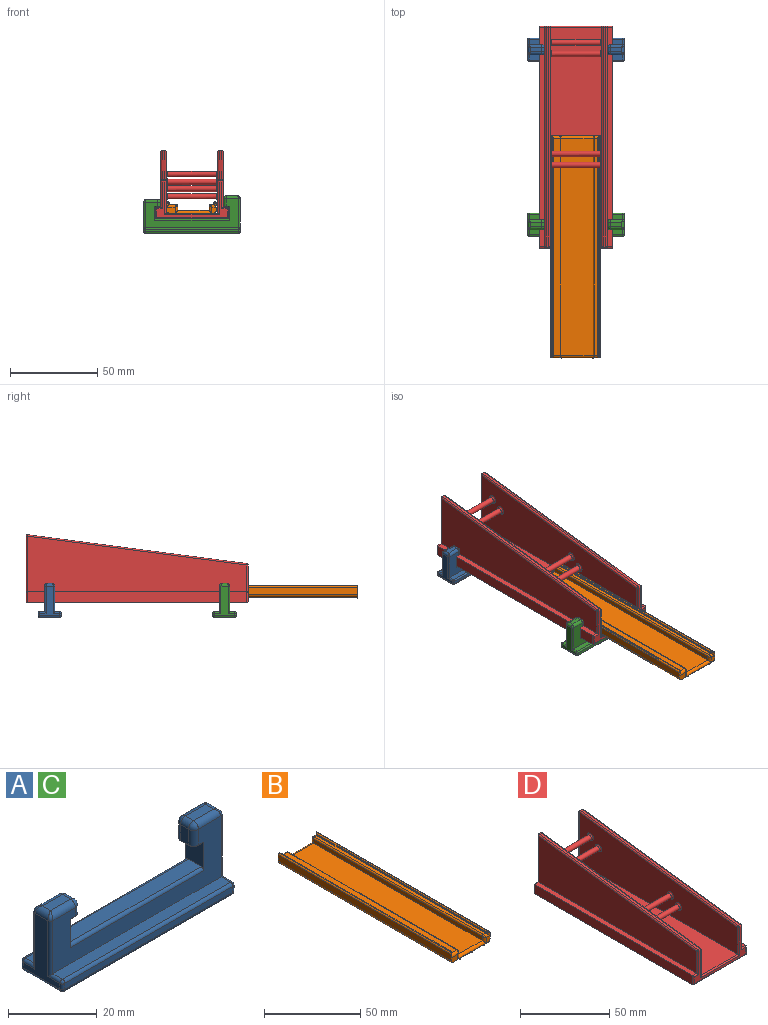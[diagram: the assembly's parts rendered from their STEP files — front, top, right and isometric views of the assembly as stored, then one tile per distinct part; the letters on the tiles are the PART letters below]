
ASSEMBLY  parts=4 mates=3
PART A: 76 faces, bbox 55.1x13.3x21.4 mm
  f0: plane 53.49x16.69mm, normal (0,-1,0), area 372.4mm2, adj f9,f11,f17,f18,f23,f28,f30,f35
  f1: plane 2.57x2.36mm, normal (1,0,0), area 6.1mm2, adj f16,f17,f21,f32
  f2: plane 6.38x2.57mm, normal (0,0,1), area 16.4mm2, adj f14,f15,f18,f21
  f3: plane 17.04x11.76mm, normal (-1,0,0), area 82.8mm2, adj f14,f45,f46,f50,f56,f59,f62,f63
  f4: plane 53.49x11.76mm, normal (0,0,-1), area 629.1mm2, adj f56,f57,f64,f65
  f5: plane 19.08x11.76mm, normal (1,0,0), area 91.2mm2, adj f29,f49,f52,f58,f65,f69,f71,f72
  f6: plane 6.38x2.57mm, normal (0,0,1), area 16.4mm2, adj f24,f27,f28,f29
  f7: plane 4.39x2.57mm, normal (-1,0,0), area 11.3mm2, adj f22,f23,f24,f37
  f8: plane 4.95x2.79mm, normal (0,0,-1), area 13.2mm2, adj f9,f35,f36,f37,f38,f39
  f9: plane 7.87x5.72mm, normal (-1,0,0), area 38.7mm2, adj f0,f8,f10,f13,f35,f39,f74,f75
  f10: plane 42.37x4.14mm, normal (0,0,1), area 175.4mm2, adj f9,f11,f74,f75
  f11: plane 7.87x5.72mm, normal (1,0,0), area 38.7mm2, adj f0,f10,f12,f13,f30,f34,f74,f75
  f12: plane 4.95x2.79mm, normal (0,0,-1), area 13.2mm2, adj f11,f30,f31,f32,f33,f34
  f13: plane 53.49x16.69mm, normal (0,1,0), area 372.4mm2, adj f9,f11,f15,f16,f22,f27,f34,f39
  f14: cylinder r=1.57mm len=4.14mm, axis (0,-1,0), area 8.8mm2, adj f2,f3,f44,f55
  f15: cylinder r=1.57mm len=7.16mm, axis (1,0,0), area 17mm2, adj f2,f13,f19,f55
  f16: cylinder r=1.57mm len=2.36mm, axis (0,0,-1), area 5.8mm2, adj f1,f13,f19,f33
  f17: cylinder r=1.57mm len=2.36mm, axis (0,0,1), area 5.8mm2, adj f0,f1,f20,f31
  f18: cylinder r=1.57mm len=7.16mm, axis (-1,0,0), area 17mm2, adj f0,f2,f20,f44
  f19: sphere r=1.57mm, area 3.9mm2, adj f15,f16,f21
  f20: sphere r=1.57mm, area 3.9mm2, adj f17,f18,f21
  f21: cylinder r=1.57mm len=2.57mm, axis (0,1,0), area 6.3mm2, adj f1,f2,f19,f20
  f22: cylinder r=1.57mm len=4.39mm, axis (0,0,1), area 10.9mm2, adj f7,f13,f25,f38
  f23: cylinder r=1.57mm len=4.39mm, axis (0,0,-1), area 10.9mm2, adj f0,f7,f26,f36
  f24: cylinder r=1.57mm len=2.57mm, axis (0,1,0), area 6.3mm2, adj f6,f7,f25,f26
  f25: sphere r=1.57mm, area 3.9mm2, adj f22,f24,f27
  f26: sphere r=1.57mm, area 3.9mm2, adj f23,f24,f28
  f27: cylinder r=1.57mm len=7.16mm, axis (1,0,0), area 17mm2, adj f6,f13,f25,f73
  f28: cylinder r=1.57mm len=7.16mm, axis (-1,0,0), area 17mm2, adj f0,f6,f26,f47
  f29: cylinder r=1.57mm len=4.14mm, axis (0,-1,0), area 8.8mm2, adj f5,f6,f47,f73
  f30: plane 1.6x0.38mm, normal (0,-0.71,-0.71), area 0.9mm2, adj f0,f11,f12,f31
  f31: cone r=1.19mm half-angle=45deg, axis (0,0,1), area 1.2mm2, adj f12,f17,f30,f32
  f32: plane 2.57x0.38mm, normal (0.71,0,-0.71), area 1.4mm2, adj f1,f12,f31,f33
  f33: cone r=1.19mm half-angle=45deg, axis (0,0,1), area 1.2mm2, adj f12,f16,f32,f34
  f34: plane 1.6x0.38mm, normal (0,0.71,-0.71), area 0.9mm2, adj f11,f12,f13,f33
  f35: plane 1.6x0.38mm, normal (0,-0.71,-0.71), area 0.9mm2, adj f0,f8,f9,f36
  f36: cone r=1.19mm half-angle=45deg, axis (0,0,1), area 1.2mm2, adj f8,f23,f35,f37
  f37: plane 2.57x0.38mm, normal (-0.71,0,-0.71), area 1.4mm2, adj f7,f8,f36,f38
  f38: cone r=1.19mm half-angle=45deg, axis (0,0,1), area 1.2mm2, adj f8,f22,f37,f39
  f39: plane 1.6x0.38mm, normal (0,0.71,-0.71), area 0.9mm2, adj f8,f9,f13,f38
  f40: plane 53.49x1.6mm, normal (0,-1,0), area 85.6mm2, adj f50,f51,f57,f58
  f41: plane 53.49x3.02mm, normal (0,0,1), area 161.7mm2, adj f0,f46,f51,f52
  f42: plane 53.49x1.6mm, normal (0,1,0), area 85.6mm2, adj f63,f64,f68,f69
  f43: plane 53.49x3.02mm, normal (0,0,1), area 161.7mm2, adj f13,f62,f68,f71
  f44: bspline ~1.88x1.57mm, area 2mm2, adj f14,f18,f45
  f45: cylinder r=0.79mm len=15.44mm, axis (0,0,-1), area 18.5mm2, adj f0,f3,f44,f46
  f46: cylinder r=0.79mm len=3.81mm, axis (0,1,0), area 4.1mm2, adj f3,f41,f45,f48
  f47: bspline ~1.88x1.58mm, area 2mm2, adj f28,f29,f49
  f48: sphere r=0.79mm, area 1mm2, adj f46,f50,f51
  f49: cylinder r=0.79mm len=17.48mm, axis (0,0,1), area 21mm2, adj f0,f5,f47,f52
  f50: cylinder r=0.79mm len=1.6mm, axis (0,0,1), area 2mm2, adj f3,f40,f48,f53
  f51: cylinder r=0.79mm len=53.49mm, axis (-1,0,0), area 66.2mm2, adj f40,f41,f48,f54
  f52: cylinder r=0.79mm len=3.81mm, axis (0,-1,0), area 4.1mm2, adj f5,f41,f49,f54
  f53: sphere r=0.79mm, area 1mm2, adj f50,f56,f57
  f54: sphere r=0.79mm, area 1mm2, adj f51,f52,f58
  f55: bspline ~1.88x1.57mm, area 2mm2, adj f14,f15,f59
  f56: cylinder r=0.79mm len=11.76mm, axis (0,-1,0), area 14.5mm2, adj f3,f4,f53,f60
  f57: cylinder r=0.79mm len=53.49mm, axis (1,0,0), area 66.2mm2, adj f4,f40,f53,f61
  f58: cylinder r=0.79mm len=1.6mm, axis (0,0,-1), area 2mm2, adj f5,f40,f54,f61
  f59: cylinder r=0.79mm len=15.44mm, axis (0,0,1), area 18.5mm2, adj f3,f13,f55,f62
  f60: sphere r=0.79mm, area 1mm2, adj f56,f63,f64
  f61: sphere r=0.79mm, area 1mm2, adj f57,f58,f65
  f62: cylinder r=0.79mm len=3.81mm, axis (0,1,0), area 4.1mm2, adj f3,f43,f59,f66
  f63: cylinder r=0.79mm len=1.6mm, axis (0,0,-1), area 2mm2, adj f3,f42,f60,f66
  f64: cylinder r=0.79mm len=53.49mm, axis (-1,0,0), area 66.2mm2, adj f4,f42,f60,f67
  f65: cylinder r=0.79mm len=11.76mm, axis (0,1,0), area 14.5mm2, adj f4,f5,f61,f67
  f66: sphere r=0.79mm, area 1mm2, adj f62,f63,f68
  f67: sphere r=0.79mm, area 1mm2, adj f64,f65,f69
  f68: cylinder r=0.79mm len=53.49mm, axis (-1,0,0), area 66.2mm2, adj f42,f43,f66,f70
  f69: cylinder r=0.79mm len=1.6mm, axis (0,0,1), area 2mm2, adj f5,f42,f67,f70
  f70: sphere r=0.79mm, area 1mm2, adj f68,f69,f71
  f71: cylinder r=0.79mm len=3.81mm, axis (0,-1,0), area 4.1mm2, adj f5,f43,f70,f72
  f72: cylinder r=0.79mm len=17.48mm, axis (0,0,-1), area 21mm2, adj f5,f13,f71,f73
  f73: bspline ~1.88x1.57mm, area 2mm2, adj f27,f29,f72
  f74: cylinder r=0.79mm len=42.37mm, axis (-1,0,0), area 52.4mm2, adj f0,f9,f10,f11
  f75: cylinder r=0.79mm len=42.37mm, axis (1,0,0), area 52.4mm2, adj f9,f10,f11,f13
PART B: 58 faces, bbox 28.5x127x6.9 mm
  f0: plane 123.85x17.78mm, normal (0,0,1), area 2202.1mm2, adj f1,f23,f32,f41
  f1: plane 123.85x2.62mm, normal (1,0,0), area 324mm2, adj f0,f26,f33,f42
  f2: plane 123.85x4.14mm, normal (0,0,1), area 512.8mm2, adj f3,f26,f36,f45
  f3: plane 123.85x0.51mm, normal (1,0,0), area 62.9mm2, adj f2,f4,f34,f43
  f4: plane 126.58x0.79mm, normal (0,0,1), area 99mm2, adj f3,f5,f34,f43
  f5: plane 126.58x0.51mm, normal (1,0,0), area 64.3mm2, adj f4,f6,f34,f43
  f6: plane 126.58x0.79mm, normal (0,0,-1), area 99mm2, adj f5,f27,f34,f43
  f7: plane 126.55x0.12mm, normal (0,0,1), area 14.9mm2, adj f27,f28,f34,f43
  f8: plane 127x3.96mm, normal (-1,0,0), area 503.2mm2, adj f24,f25,f28,f34,f43,f50
  f9: plane 127x4.11mm, normal (0,0,-1), area 521.7mm2, adj f24,f25,f50,f52
  f10: cylinder r=0.55mm len=127mm, axis (0,-1,0), area 159.1mm2, adj f24,f25,f52,f53
  f11: plane 127x7.2mm, normal (0,0,-1), area 914.4mm2, adj f24,f25,f53,f54
  f12: cylinder r=0.55mm len=127mm, axis (0,-1,0), area 159.1mm2, adj f24,f25,f54,f55
  f13: plane 127x7.2mm, normal (0,0,-1), area 914.4mm2, adj f24,f25,f55,f56
  f14: cylinder r=0.55mm len=127mm, axis (0,-1,0), area 159.1mm2, adj f24,f25,f56,f57
  f15: plane 127x1.82mm, normal (0,0,-1), area 231.4mm2, adj f24,f25,f51,f57
  f16: plane 127x3.96mm, normal (1,0,0), area 503.2mm2, adj f24,f25,f29,f37,f46,f51
  f17: plane 126.55x0.12mm, normal (0,0,1), area 14.9mm2, adj f29,f30,f37,f46
  f18: plane 126.58x0.79mm, normal (0,0,-1), area 99mm2, adj f19,f30,f37,f46
  f19: plane 126.58x0.51mm, normal (-1,0,0), area 64.3mm2, adj f18,f20,f37,f46
  f20: plane 126.58x0.79mm, normal (0,0,1), area 99mm2, adj f19,f21,f37,f46
  f21: plane 123.85x0.51mm, normal (-1,0,0), area 62.9mm2, adj f20,f22,f37,f46
  f22: plane 123.85x1.85mm, normal (0,0,1), area 229.6mm2, adj f21,f31,f38,f49
  f23: plane 123.85x2.62mm, normal (-1,0,0), area 324mm2, adj f0,f31,f40,f47
  f24: plane 28.55x3.99mm, normal (0,1,0), area 26.9mm2, adj f8,f9,f10,f11,f12,f13,f14,f15
  f25: plane 28.55x3.99mm, normal (0,-1,0), area 26.9mm2, adj f8,f9,f10,f11,f12,f13,f14,f15
  f26: cylinder r=0.81mm len=123.85mm, axis (0,-1,0), area 158.1mm2, adj f1,f2,f35,f44
  f27: cylinder r=0.81mm len=126.39mm, axis (0,1,0), area 93.4mm2, adj f6,f7,f34,f43
  f28: cylinder r=0.81mm len=127mm, axis (0,-1,0), area 162mm2, adj f7,f8,f34,f43
  f29: cylinder r=0.81mm len=127mm, axis (0,-1,0), area 162mm2, adj f16,f17,f37,f46
  f30: cylinder r=0.81mm len=126.39mm, axis (0,1,0), area 93.4mm2, adj f17,f18,f37,f46
  f31: cylinder r=0.81mm len=123.85mm, axis (0,-1,0), area 158.1mm2, adj f22,f23,f39,f48
  f32: cylinder r=1.57mm len=20.93mm, axis (1,0,0), area 46.8mm2, adj f0,f24,f33,f47
  f33: cylinder r=1.57mm len=4.19mm, axis (0,0,-1), area 7.2mm2, adj f1,f24,f32,f35
  f34: cylinder r=1.57mm len=2.91mm, axis (0,0,-1), area 3.5mm2, adj f3,f4,f5,f6,f7,f8,f27,f28
  f35: bspline ~1.65x1.58mm, area 2.1mm2, adj f26,f33,f36
  f36: cylinder r=1.57mm len=5.72mm, axis (1,0,0), area 11mm2, adj f2,f24,f34,f35
  f37: cylinder r=1.57mm len=2.91mm, axis (0,0,-1), area 3.5mm2, adj f16,f17,f18,f19,f20,f21,f29,f30
  f38: cylinder r=1.57mm len=3.43mm, axis (-1,0,0), area 5.3mm2, adj f22,f25,f37,f39
  f39: bspline ~1.65x1.58mm, area 2.1mm2, adj f31,f38,f40
  f40: cylinder r=1.57mm len=4.19mm, axis (0,0,-1), area 7.2mm2, adj f23,f25,f39,f41
  f41: cylinder r=1.57mm len=20.93mm, axis (-1,0,0), area 46.8mm2, adj f0,f25,f40,f42
  f42: cylinder r=1.57mm len=4.19mm, axis (0,0,1), area 7.2mm2, adj f1,f25,f41,f44
  f43: cylinder r=1.57mm len=2.91mm, axis (0,0,1), area 3.5mm2, adj f3,f4,f5,f6,f7,f8,f27,f28
  f44: bspline ~1.65x1.58mm, area 2.1mm2, adj f26,f42,f45
  f45: cylinder r=1.57mm len=5.72mm, axis (-1,0,0), area 11mm2, adj f2,f25,f43,f44
  f46: cylinder r=1.57mm len=2.91mm, axis (0,0,1), area 3.5mm2, adj f16,f17,f18,f19,f20,f21,f29,f30
  f47: cylinder r=1.57mm len=4.19mm, axis (0,0,1), area 7.2mm2, adj f23,f24,f32,f48
  f48: bspline ~1.65x1.58mm, area 2.1mm2, adj f31,f47,f49
  f49: cylinder r=1.57mm len=3.43mm, axis (1,0,0), area 5.3mm2, adj f22,f24,f46,f48
  f50: cylinder r=1.57mm len=127mm, axis (0,1,0), area 314.2mm2, adj f8,f9,f24,f25
  f51: cylinder r=1.57mm len=127mm, axis (0,1,0), area 314.2mm2, adj f15,f16,f24,f25
  f52: cylinder r=0.38mm len=127mm, axis (0,-1,0), area 55.5mm2, adj f9,f10,f24,f25
  f53: cylinder r=0.38mm len=127mm, axis (0,-1,0), area 55.5mm2, adj f10,f11,f24,f25
  f54: cylinder r=0.38mm len=127mm, axis (0,-1,0), area 55.5mm2, adj f11,f12,f24,f25
  f55: cylinder r=0.38mm len=127mm, axis (0,-1,0), area 55.5mm2, adj f12,f13,f24,f25
  f56: cylinder r=0.38mm len=127mm, axis (0,-1,0), area 55.5mm2, adj f13,f14,f24,f25
  f57: cylinder r=0.38mm len=127mm, axis (0,-1,0), area 55.5mm2, adj f14,f15,f24,f25
PART C: same geometry as A
PART D: 61 faces, bbox 42x127x38.8 mm
  f0: plane 125.37x6.35mm, normal (-1,0,0), area 796.1mm2, adj f1,f9,f28,f32
  f1: plane 125.37x42.01mm, normal (0,0,-1), area 5267.2mm2, adj f0,f2,f24,f27
  f2: plane 126.19x6.35mm, normal (1,0,0), area 801mm2, adj f1,f3,f10,f18,f23,f24
  f3: plane 125.37x3.18mm, normal (0,0,1), area 398.1mm2, adj f2,f4,f18,f19
  f4: plane 125.37x31.67mm, normal (1,0,0), area 2935.7mm2, adj f3,f20,f21,f22
  f5: plane 125.37x34.84mm, normal (-1,0,0), area 3261.3mm2, adj f6,f30,f38,f39,f53,f55,f57,f59
  f6: plane 125.37x29.31mm, normal (0,0,1), area 3674.9mm2, adj f5,f7,f43,f44
  f7: plane 125.37x34.84mm, normal (1,0,0), area 3261.3mm2, adj f6,f47,f48,f52,f54,f56,f58,f60
  f8: plane 125.37x31.67mm, normal (-1,0,0), area 2935.7mm2, adj f9,f37,f40,f41
  f9: plane 125.37x3.18mm, normal (0,0,1), area 398.1mm2, adj f0,f8,f33,f36
  f10: plane 41.2x37.21mm, normal (0,1,0), area 197.1mm2, adj f2,f18,f20,f24,f28,f29,f33,f37
  f11: plane 40.39x20.7mm, normal (0,-1,0), area 142.1mm2, adj f19,f22,f23,f27,f31,f32,f36,f39
  f12: cylinder r=1.59mm len=27.69mm, axis (-1,0,0), area 276.2mm2, adj f59,f60
  f13: cylinder r=1.59mm len=27.69mm, axis (-1,0,0), area 276.2mm2, adj f57,f58
  f14: cylinder r=1.59mm len=27.69mm, axis (-1,0,0), area 276.2mm2, adj f55,f56
  f15: cylinder r=1.59mm len=27.69mm, axis (-1,0,0), area 276.2mm2, adj f53,f54
  f16: plane 125.37x16.51mm, normal (0,-0.13,0.99), area 195.9mm2, adj f21,f29,f30,f31
  f17: plane 125.37x16.51mm, normal (0,-0.13,0.99), area 195.9mm2, adj f41,f46,f49,f52
  f18: cylinder r=0.81mm len=3.99mm, axis (1,0,0), area 4.4mm2, adj f2,f3,f10,f20
  f19: cylinder r=0.81mm len=3.99mm, axis (-1,0,0), area 4.1mm2, adj f3,f11,f22,f23
  f20: cylinder r=0.81mm len=32.48mm, axis (0,0,-1), area 40.8mm2, adj f4,f10,f18,f25
  f21: cylinder r=0.81mm len=125.48mm, axis (0,-0.99,-0.13), area 161.5mm2, adj f4,f16,f25,f26
  f22: cylinder r=0.81mm len=15.98mm, axis (0,0,1), area 19.7mm2, adj f4,f11,f19,f26
  f23: cylinder r=0.81mm len=6.35mm, axis (0,0,1), area 7.4mm2, adj f2,f11,f19,f27
  f24: cylinder r=0.81mm len=42.01mm, axis (-1,0,0), area 53.3mm2, adj f1,f2,f10,f28
  f25: sphere r=0.81mm, area 1.1mm2, adj f20,f21,f29
  f26: sphere r=0.81mm, area 1mm2, adj f21,f22,f31
  f27: cylinder r=0.81mm len=42.01mm, axis (1,0,0), area 52.9mm2, adj f1,f11,f23,f32
  f28: cylinder r=0.81mm len=6.35mm, axis (0,0,1), area 7.4mm2, adj f0,f10,f24,f33
  f29: cylinder r=0.81mm len=1.55mm, axis (1,0,0), area 2.1mm2, adj f10,f16,f25,f34
  f30: cylinder r=0.81mm len=125.48mm, axis (0,0.99,0.13), area 161.5mm2, adj f5,f16,f34,f35
  f31: cylinder r=0.81mm len=1.55mm, axis (-1,0,0), area 1.8mm2, adj f11,f16,f26,f35
  f32: cylinder r=0.81mm len=6.35mm, axis (0,0,-1), area 7.4mm2, adj f0,f11,f27,f36
  f33: cylinder r=0.81mm len=3.99mm, axis (1,0,0), area 4.1mm2, adj f9,f10,f28,f37
  f34: sphere r=0.81mm, area 1.1mm2, adj f29,f30,f38
  f35: sphere r=0.81mm, area 1mm2, adj f30,f31,f39
  f36: cylinder r=0.81mm len=3.99mm, axis (-1,0,0), area 4.1mm2, adj f9,f11,f32,f40
  f37: cylinder r=0.81mm len=32.48mm, axis (0,0,1), area 40.8mm2, adj f8,f10,f33,f42
  f38: cylinder r=0.81mm len=35.66mm, axis (0,0,1), area 44.9mm2, adj f5,f10,f34,f43
  f39: cylinder r=0.81mm len=19.15mm, axis (0,0,-1), area 23.8mm2, adj f5,f11,f35,f44
  f40: cylinder r=0.81mm len=15.98mm, axis (0,0,-1), area 19.7mm2, adj f8,f11,f36,f45
  f41: cylinder r=0.81mm len=125.48mm, axis (0,0.99,0.13), area 161.5mm2, adj f8,f17,f42,f45
  f42: sphere r=0.81mm, area 1.1mm2, adj f37,f41,f46
  f43: cylinder r=0.81mm len=30.94mm, axis (1,0,0), area 38.2mm2, adj f6,f10,f38,f47
  f44: cylinder r=0.81mm len=30.94mm, axis (-1,0,0), area 38.2mm2, adj f6,f11,f39,f48
  f45: sphere r=0.81mm, area 1mm2, adj f40,f41,f49
  f46: cylinder r=0.81mm len=1.55mm, axis (1,0,0), area 2.1mm2, adj f10,f17,f42,f50
  f47: cylinder r=0.81mm len=35.66mm, axis (0,0,-1), area 44.9mm2, adj f7,f10,f43,f50
  f48: cylinder r=0.81mm len=19.15mm, axis (0,0,1), area 23.8mm2, adj f7,f11,f44,f51
  f49: cylinder r=0.81mm len=1.55mm, axis (-1,0,0), area 1.8mm2, adj f11,f17,f45,f51
  f50: sphere r=0.81mm, area 1.1mm2, adj f46,f47,f52
  f51: sphere r=0.81mm, area 1mm2, adj f48,f49,f52
  f52: cylinder r=0.81mm len=125.48mm, axis (0,-0.99,-0.13), area 161.5mm2, adj f7,f17,f50,f51
  f53: torus R=2.4mm, axis (1,0,0), area 15.1mm2, adj f5,f15
  f54: torus R=2.4mm, axis (-1,0,0), area 15.1mm2, adj f7,f15
  f55: torus R=2.4mm, axis (1,0,0), area 15.1mm2, adj f5,f14
  f56: torus R=2.4mm, axis (-1,0,0), area 15.1mm2, adj f7,f14
  f57: torus R=2.4mm, axis (1,0,0), area 15.1mm2, adj f5,f13
  f58: torus R=2.4mm, axis (-1,0,0), area 15.1mm2, adj f7,f13
  f59: torus R=2.4mm, axis (1,0,0), area 15.1mm2, adj f5,f12
  f60: torus R=2.4mm, axis (-1,0,0), area 15.1mm2, adj f7,f12
PLACE A t=(1.71,73.59,23.51)mm
PLACE B t=(1.41,-99.73,22.95)mm
PLACE C t=(1.71,-26.39,23.51)mm
PLACE D t=(1.71,-37.04,23.33)mm fixed
MATE fastened D.f6 <-> B.f11  axis (0,0,1) through (0.57,-36.23,22.95)mm
MATE fastened C.f10 <-> D.f1  axis (0,0,1) through (0.57,-23.53,19.78)mm
MATE fastened A.f10 <-> D.f1  axis (0,0,1) through (0.57,76.44,19.78)mm
